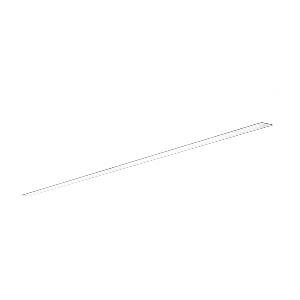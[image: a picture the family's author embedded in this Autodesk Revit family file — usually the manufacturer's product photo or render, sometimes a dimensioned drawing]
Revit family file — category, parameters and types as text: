
# Revit family: dotoo_line_-_dle_3000_840_d_00808225_f8d6
name_source: partatom
category: Lighting Fixtures
units: mm (PartAtom-declared; Revit-internal decimal feet)

## family parameters
Cut with Voids When Loaded = No
Host = Face
Light Source = No
Part Type = Normal
Room Calculation Point = No
Round Connector Dimension = Use Diameter
Shared = No

## types (1)
- DOTOO.line - DLE 3000/840/D (1 x LED, 2750 lm, 4000K)
    Apparent Load = 26 VA
    Approval mark = CE
    CIE Flux Codes = 67 91 98 100 100
    Color Rendering = 80-89
    Color Temperature = 4000K
    Control Gear = Electronic ballast
    Default Elevation = 1800 mm
    Description = DLE 3000/840/D|Recessed luminaire|light source:  |work equipment: Adjustable electronic ballast, digital DALI|connected load: 220-240 V, 50/60 Hz|Power consumption: approx. 26 W|standby: approx. 0,20|power factor: approx. 0,970|luminous flux: 2750 lm|luminous efficacy: 105 lm/W|light distribution: Direct|direct ratio: approx. 100 %|colour temperature: Cold white, ca. 4000 K|color rendering index (CRI): >= 80|chromaticity tolerance:  3 SDCM|System of protection: IP 40|class of protection: I|technology: Continuously dimmable|operation: External|luminaire body|material: Sectional aluminium|colour: White|lamp cover: Acrylic (PMMA), Clear|weight (net): approx. 7.3 kg|mains lead: Connector|Fastening: Fastening bow|glare control: Prism aperture|luminance(L65): <= 3000 cd/m|unified glare rating(4H 8H): <=  19|special features: DALI Load 1x, TouchDIM - dimming via standard switch, Flicker-free, Suitable as emergency lighting|
    Frequency = 50 Hz
    Height = 0 mm  [stored 0 ft]
    Lamp = 1 x LED
    Lamp Light Flux = 2750 lm
    Lamp count = 1
    Length = 2256 mm
    Luminous efficacy = 106 lm/W
    Manufacturer = Waldmann
    ModVariant = No
    Model = 00808225
    Mounting Place = Ceiling
    Mounting Type = Recessed
    Number of Poles = 1
    OnlyDefault = Yes
    Power Factor = 1
    Product Name = DOTOO.line - DLE 3000/840/D
    Product group = Recessed luminaire
    ProductGroupID = 4
    Protection Class = Protection class I
    Protection Degree = IP 40
    RLX_Detail_Level = 1
    RLX_Emergency_Light_Flux = 0 lm
    RLX_Emergency_Type = 0
    RLX_Emergency_Type_DB = No
    RlxData = <blob elided: 14661 chars, md5=e5181080>
    Socket = socket
    Standby Power = 0 W
    System Light Flux = 2750 lm
    System Power = 26 W
    Type Comments = Product without accessories
    Type Image = 114407000-00808225.jpg
    URL = http://relux.com
    VarID = ---
    Voltage = 230 V
    Voltage Range = 220-240 V
    Weight = 0.00 kg
    Width = 60 mm  [stored 0.19685 ft]

note: [stored X ft] marks values corroborated as IEEE doubles in the binary element streams (Revit-internal decimal feet)

## geometry (parser evidence)
native form markers: Sweep x12
no freeform markers — native parametric forms only
